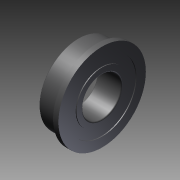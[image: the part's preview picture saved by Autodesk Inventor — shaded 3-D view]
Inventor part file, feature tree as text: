
AUTODESK INVENTOR PART (.ipt)
format: ipt  version: 2011 SP1 (Build 150282100, 282)  size: 153,600 bytes
history: native  units: mm
features: other x7, revolve x1, sketch x1
ambient origin geometry x8: Origin, YZ Plane, XZ Plane, XY Plane, X Axis, Y Axis, Z Axis, Center Point
bodies: Solid1 (feature_tree)
feature tree (9):
  revolve  "Revolution1"  [1 undecoded]
  other  "to_housing_XY"
  other  "to_housing_YZ"
  other  "to_housing_ZX"
  other  "to_housing_X"
  other  "to_housing_Y"
  other  "to_housing_Z"
  other  "to_housing_Center"
  sketch  "Sketch_1"  dims[d0=360.0deg d1=0.0mm]
note: 1 required parameter value undecoded (feature->parameter linkage not recoverable at this tier; creation-order binding heuristic only, values carry confidence <= 0.55)
